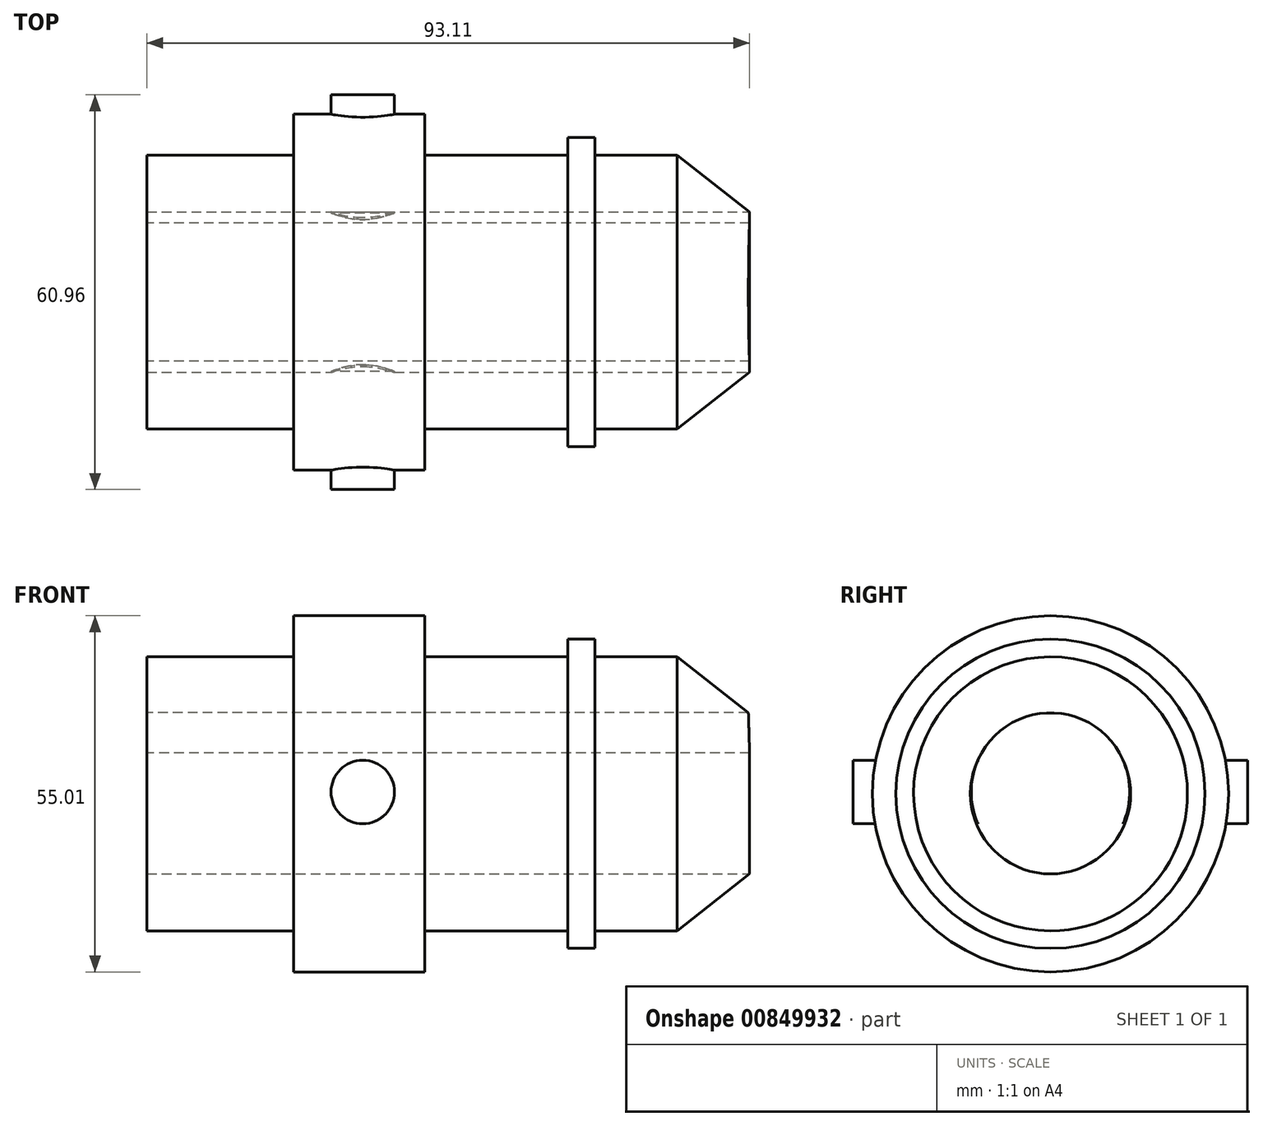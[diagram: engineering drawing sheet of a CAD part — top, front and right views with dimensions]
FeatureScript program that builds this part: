
annotation { "Feature Type Name" : "Feature", "Feature Type Description" : "" }
export const myFeature = defineFeature(function(context is Context, id is Id, definition is map)
    precondition{}
    {
        {
            var Q0;
            Q0=qCreatedBy(makeId("Front.planeOp"),FACE);
            var sketch = newSketch(context, id + "F0", { "sketchPlane" : qUnion([Q0])});
            skLineSegment(sketch, "E0", {"start": v(0, 0) * mm, "end": v(22.64, 0) * mm});
            skLineSegment(sketch, "E1", {"start": v(22.64, 0) * mm, "end": v(22.64, -6.35) * mm});
            skLineSegment(sketch, "E2", {"start": v(22.64, -6.35) * mm, "end": v(42.91, -6.35) * mm});
            skLineSegment(sketch, "E3", {"start": v(42.91, -6.35) * mm, "end": v(42.91, 0) * mm});
            skLineSegment(sketch, "E4", {"start": v(42.91, 0) * mm, "end": v(65, 0) * mm});
            skLineSegment(sketch, "E5", {"start": v(65, 0) * mm, "end": v(65, -2.72) * mm});
            skLineSegment(sketch, "E6", {"start": v(65, -2.72) * mm, "end": v(69.22, -2.72) * mm});
            skLineSegment(sketch, "E7", {"start": v(69.22, -2.72) * mm, "end": v(69.22, 0) * mm});
            skLineSegment(sketch, "E8", {"start": v(69.22, 0) * mm, "end": v(81.88, 0) * mm});
            skLineSegment(sketch, "E9", {"start": v(93.1, 8.78) * mm, "end": v(0, 8.78) * mm});
            skLineSegment(sketch, "E10", {"start": v(81.88, 0) * mm, "end": v(93.1, 8.78) * mm});
            skLineSegment(sketch, "E11", {"start": v(0, 0) * mm, "end": v(0, 8.78) * mm});
            skLineSegment(sketch, "E12", {"start": v(0, 21.15) * mm, "end": v(97.42, 21.15) * mm, "construction": true});
            skSolve(sketch);
        }
        {
            var Q0;
            Q0=makeQuery(id+"F0.imprint","IMPRINT",FACE,{"disambiguationData":[TD([[makeQuery(id+"F0.imprint","IMPRINT",EDGE,{"derivedFrom":sQuery(id+"F0.wireOp",EDGE,"E0")}),1.0]])]});
            var Q1;
            Q1=sQuery(id+"F0.wireOp",EDGE,"E12");
            revolve(context, id + "F1", {"surfaceOperationType" : NewSurfaceOperationType.NEW, "entities" : qUnion([Q0]), "axis" : qUnion([Q1]), "revolveType" : RevolveType.ONE_DIRECTION, "oppositeDirection" : true, "angle" : 360 * degree});
        }
        {
            var Q0;
            Q0=qCreatedBy(makeId("Front.planeOp"),FACE);
            var sketch = newSketch(context, id + "F2", { "sketchPlane" : qUnion([Q0])});
            skCircle(sketch, "E13", {"center": v(33.35, 21.44) * mm, "radius": 4.9 * mm});
            skSolve(sketch);
        }
        {
            var Q0;
            Q0 = qSketchRegion(id + "F2", true);
            extrude(context, id + "F3", {"entities" : qUnion([Q0]), "operationType" : NewBodyOperationType.ADD, "oppositeDirection" : true, "depth" : 30.48 * mm, "offsetDistance" : 25.4 * mm, "hasSecondDirection" : true, "secondDirectionOppositeDirection" : false, "secondDirectionDepth" : 30.48 * mm});
        }
        {
            var Q0;
            Q0=qCreatedBy(makeId("Right.planeOp"),FACE);
            var sketch = newSketch(context, id + "F4", { "sketchPlane" : qUnion([Q0])});
            skCircle(sketch, "E14", {"center": v(0, 21.44) * mm, "radius": 12.23 * mm});
            skSolve(sketch);
        }
        {
            var Q0;
            Q0 = qSketchRegion(id + "F4", true);
            extrude(context, id + "F5", {"entities" : qUnion([Q0]), "operationType" : NewBodyOperationType.REMOVE, "depth" : 97.28 * mm, "offsetDistance" : 25.4 * mm});
        }
    });
